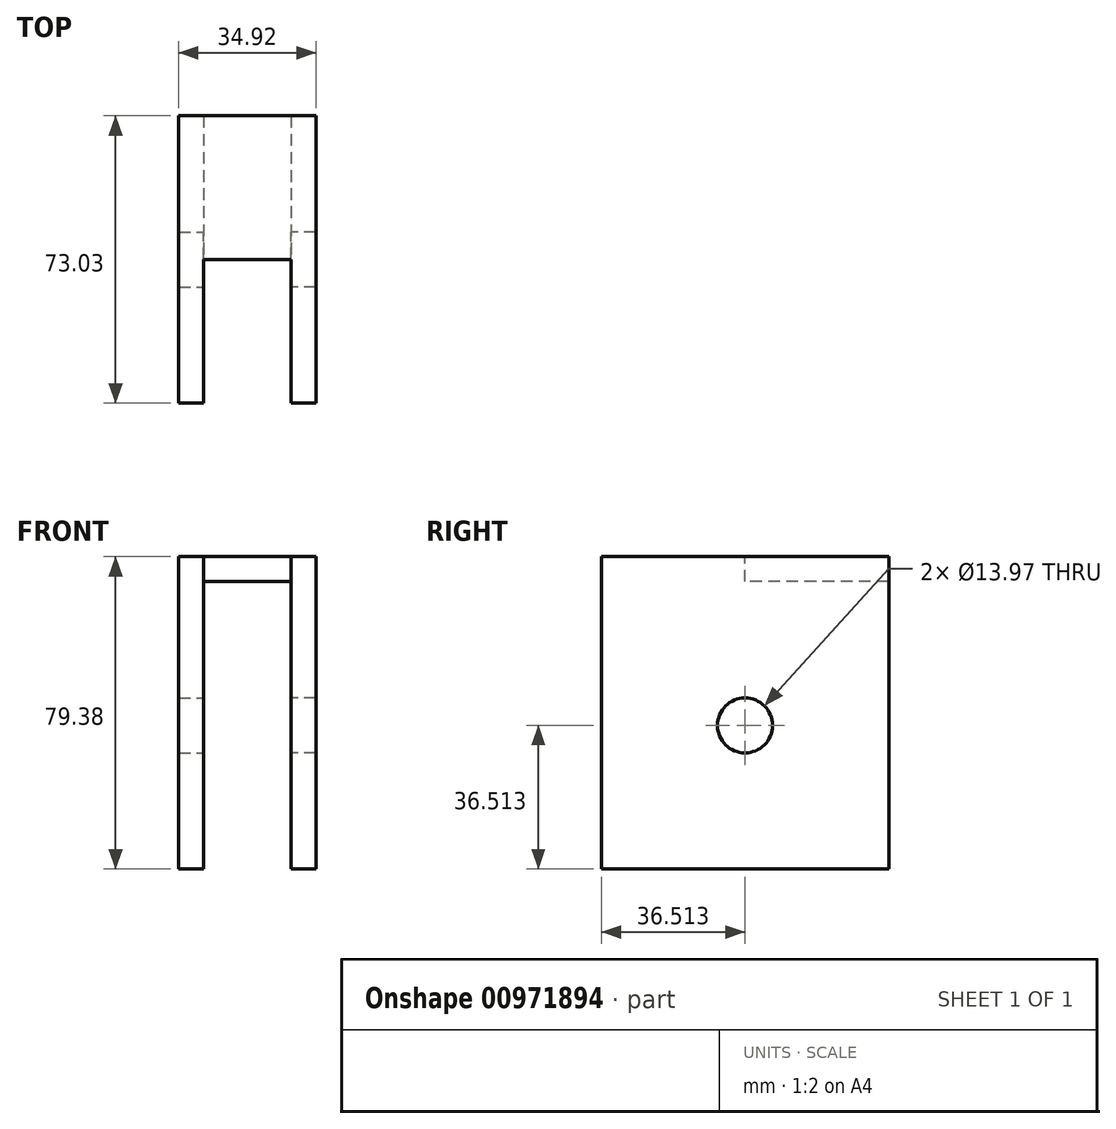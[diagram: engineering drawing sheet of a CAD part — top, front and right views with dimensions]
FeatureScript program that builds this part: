
annotation { "Feature Type Name" : "Feature", "Feature Type Description" : "" }
export const myFeature = defineFeature(function(context is Context, id is Id, definition is map)
    precondition{}
    {
        {
            var Q0;
            Q0=qCreatedBy(makeId("Front.planeOp"),FACE);
            var sketch = newSketch(context, id + "F0", { "sketchPlane" : qUnion([Q0])});
            skLineSegment(sketch, "E0.bottom", {"start": v(-11.11, 0) * mm, "end": v(-17.46, 0) * mm});
            skLineSegment(sketch, "E0.top", {"start": v(0, 79.38) * mm, "end": v(-17.46, 79.38) * mm});
            skLineSegment(sketch, "E0.left", {"start": v(0, 73.03) * mm, "end": v(0, 79.38) * mm});
            skLineSegment(sketch, "E0.right", {"start": v(-17.46, 0) * mm, "end": v(-17.46, 79.38) * mm});
            skLineSegment(sketch, "E1.top", {"start": v(0, 73.03) * mm, "end": v(-11.11, 73.03) * mm});
            skLineSegment(sketch, "E1.right", {"start": v(-11.11, 0) * mm, "end": v(-11.11, 73.03) * mm});
            skSolve(sketch);
        }
        {
            var Q0;
            Q0=qSketchRegion(id+"F0",true);
            extrude(context, id + "F1", {"entities" : qUnion([Q0]), "oppositeDirection" : true, "depth" : 73.02 * mm, "offsetDistance" : 25.4 * mm});
        }
        {
            var Q0;
            Q0=makeQuery(id+"F1.opExtrude","SWEPT_FACE",FACE,{"disambiguationData":[OSD([sQuery(id+"F0.wireOp",EDGE,"E1.right")])]});
            var sketch = newSketch(context, id + "F2", { "sketchPlane" : qUnion([Q0])});
            skCircle(sketch, "E2", {"center": v(36.51, 36.51) * mm, "radius": 6.99 * mm});
            skSolve(sketch);
        }
        {
            var Q0;
            Q0=qSketchRegion(id+"F2",true);
            extrude(context, id + "F3", {"entities" : qUnion([Q0]), "operationType" : NewBodyOperationType.REMOVE, "oppositeDirection" : true, "depth" : 25.4 * mm, "offsetDistance" : 25.4 * mm});
        }
        {
            var Q0;
            Q0=makeQuery(id+"F1.opExtrude","SWEPT_BODY",BODY,{"disambiguationData":[OSD([sQuery(id+"F0.wireOp",EDGE,"E0.bottom"),sQuery(id+"F0.wireOp",EDGE,"E0.top"),sQuery(id+"F0.wireOp",EDGE,"E0.left"),sQuery(id+"F0.wireOp",EDGE,"E0.right"),sQuery(id+"F0.wireOp",EDGE,"E1.top"),sQuery(id+"F0.wireOp",EDGE,"E1.right")])]});
            var Q1;
            Q1=qCreatedBy(makeId("Right.planeOp"),FACE);
            mirror(context, id + "F4", {"operationType" : NewBodyOperationType.ADD, "entities" : qUnion([Q0]), "mirrorPlane" : qUnion([Q1])});
        }
        {
            var Q0;
            {var subQ0=makeQuery(id+"F1.opExtrude","SWEPT_FACE",FACE,{"disambiguationData":[OSD([sQuery(id+"F0.wireOp",EDGE,"E0.top")])]});Q0=makeQuery(id+"F4.boolean.opBoolean","MERGE",FACE,{"derivedFrom":[subQ0,makeQuery(id+"F4.opPattern","COPY",FACE,{"derivedFrom":subQ0,"instanceName":"1"})]});}
            var sketch = newSketch(context, id + "F5", { "sketchPlane" : qUnion([Q0])});
            skLineSegment(sketch, "E3.bottom", {"start": v(-11.11, 0) * mm, "end": v(11.11, 0) * mm});
            skLineSegment(sketch, "E3.top", {"start": v(-11.11, 36.51) * mm, "end": v(11.11, 36.51) * mm});
            skLineSegment(sketch, "E3.left", {"start": v(-11.11, 0) * mm, "end": v(-11.11, 36.51) * mm});
            skLineSegment(sketch, "E3.right", {"start": v(11.11, 0) * mm, "end": v(11.11, 36.51) * mm});
            skSolve(sketch);
        }
        {
            var Q0;
            Q0=qSketchRegion(id+"F5",true);
            extrude(context, id + "F6", {"entities" : qUnion([Q0]), "operationType" : NewBodyOperationType.REMOVE, "oppositeDirection" : true, "depth" : 25.4 * mm, "offsetDistance" : 25.4 * mm});
        }
    });
